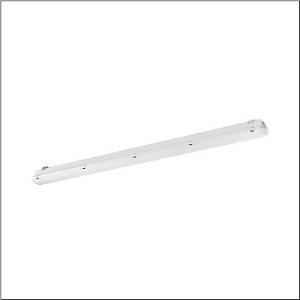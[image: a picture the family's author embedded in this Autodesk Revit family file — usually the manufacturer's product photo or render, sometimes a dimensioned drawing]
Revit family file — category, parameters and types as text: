
# Revit family: monsun_r__11xtreme_ho_51fe10dp480r_f689
name_source: partatom
category: Lighting Fixtures
units: mm (PartAtom-declared; Revit-internal decimal feet)

## family parameters
Cut with Voids When Loaded = No
Host = Face
Light Source = No
Part Type = Normal
Room Calculation Point = No
Round Connector Dimension = Use Diameter
Shared = No

## types (1)
- --- (1 x LED, 8000 lm, 44.3 W, 4000K)
    Apparent Load = 44 VA
    CIE Flux Codes = 47 76 93 94 100
    Color Rendering = 80
    Color Temperature = 4000K
    Default Elevation = 1800 mm
    Description = Monsun® 11Xtreme HO, damp-proof luminaire, chain hanger, primary optical cover: enclosure, of PMMA, light emission: direct distribution, primary light characteristic: symmetric, installation type: suspended mounting, surface-mounted, horizontal mounting, vertical mounting, LED, rated luminous flux: 8.000lm, luminous efficacy: 181lm/W, light colour: 840, colour temperature: 4000K, control gear: ECG DALI, with terminal, 5-pole, max. 2.5mm², mains connection: 220..240V, AC, 50/60Hz, rated input power: 44W, luminaire housing, of glass-fibre reinforced polyester, uncoated, bright grey, length: 1.590mm, width: 90mm, height: 88mm, clip for enclosure, of stainless steel (V2A), ceiling mounting element, of stainless steel (V2A), chain hanger, of stainless steel (V2A), protection rating (complete): IP66, insulation class (complete): insulation class I (protective earthing), certification: CE, ENEC, VDE, UKCA, protection symbol: D, impact resistance: IK04, permissible operating ambient temperature: -35..+55°C, standard: EN 60598-2-1, EN 50419, corresponds to IFS (International Featured Standards) requirements for safety and quality in the food industry, for indoor or canopied outdoor use, no direct snow, no direct sun, no direct rain, packaging unit: 1 piece
    Height = 88 mm
    Lamp = 1 x LED
    Lamp Light Flux = 8000 lm
    Lamp Power = 44.3 W
    Lamp count = 1
    Length = 1590 mm
    Luminous efficacy = 181 lm/W
    Manufacturer = Siteco
    ModVariant = No
    Model = 51FE10DP480R
    Mounting Place = Ceiling
    Mounting Type = Pendant
    Number of Poles = 1
    OnlyDefault = Yes
    Power Factor = 1
    Product Name = Monsun® 11Xtreme HO
    Product group = damp-proof luminaire | ceiling pendant
    ProductGroupID = 908
    Protection Class = Protection class I
    Protection Degree = IP 66
    RLX_Detail_Level = 1
    RlxData = <blob elided: 87301 chars, md5=92d39eab>
    Socket = socket
    Standby Power = 0 W
    System Light Flux = 8000 lm
    System Power = 44 W
    Type Comments = factory setting: luminous flux: 100 % | dim-lin: 254 | 253 mA
    Type Image = l_1006851.jpg
    URL = http://relux.com
    VarID = @adj_121221
    Voltage = 0 V
    Weight = 0.00 kg
    Width = 90 mm

## geometry (parser evidence)
native form markers: Blend x4, Sweep x13
no freeform markers — native parametric forms only
